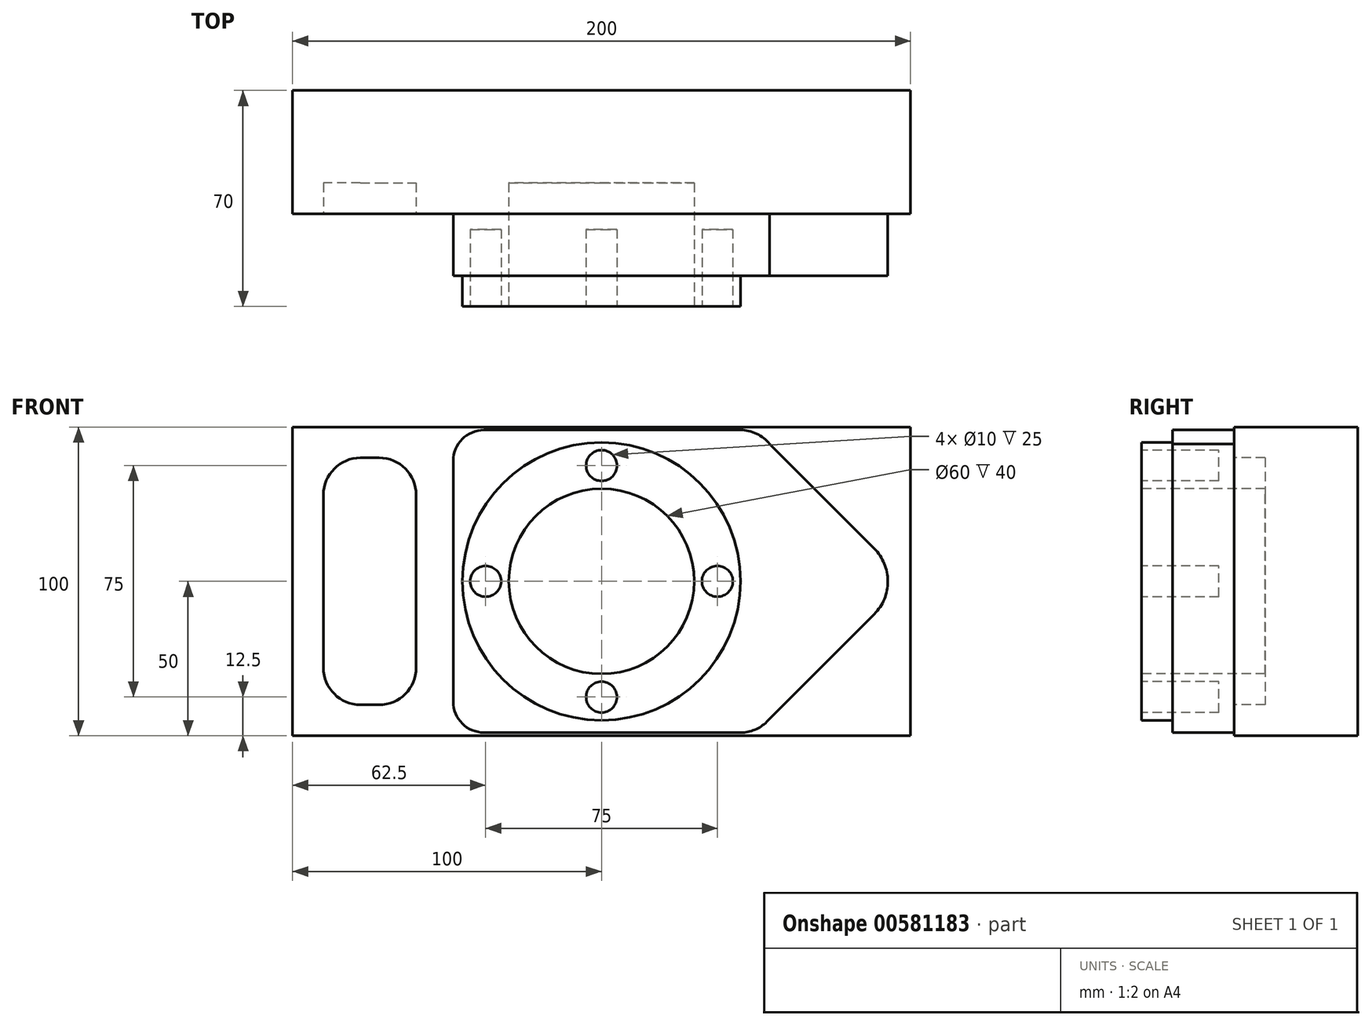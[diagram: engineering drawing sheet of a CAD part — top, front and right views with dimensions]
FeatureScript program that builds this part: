
annotation { "Feature Type Name" : "Feature", "Feature Type Description" : "" }
export const myFeature = defineFeature(function(context is Context, id is Id, definition is map)
    precondition{}
    {
        {
            var Q0;
            Q0=qCreatedBy(makeId("Front.planeOp"),FACE);
            var sketch = newSketch(context, id + "F0", { "sketchPlane" : qUnion([Q0])});
            skLineSegment(sketch, "E0.bottom", {"start": v(0, 0) * mm, "end": v(-200, 0) * mm});
            skLineSegment(sketch, "E0.top", {"start": v(0, 100) * mm, "end": v(-200, 100) * mm});
            skLineSegment(sketch, "E0.left", {"start": v(0, 0) * mm, "end": v(0, 100) * mm});
            skLineSegment(sketch, "E0.right", {"start": v(-200, 0) * mm, "end": v(-200, 100) * mm});
            skSolve(sketch);
        }
        {
            var Q0;
            Q0=makeQuery(id+"F0.imprint","IMPRINT",FACE,{"disambiguationData":[TD([[makeQuery(id+"F0.imprint","IMPRINT",EDGE,{"derivedFrom":sQuery(id+"F0.wireOp",EDGE,"E0.bottom")}),-1.0]])]});
            extrude(context, id + "F1", {"entities" : qUnion([Q0]), "depth" : 40 * mm, "offsetDistance" : 25 * mm});
        }
        {
            var Q0;
            Q0=makeQuery(id+"F1.opExtrude","CAP_FACE",FACE,{"disambiguationData":[OSD([sQuery(id+"F0.wireOp",EDGE,"E0.bottom"),sQuery(id+"F0.wireOp",EDGE,"E0.top"),sQuery(id+"F0.wireOp",EDGE,"E0.left"),sQuery(id+"F0.wireOp",EDGE,"E0.right")])],"isStart":false});
            var sketch = newSketch(context, id + "F2", { "sketchPlane" : qUnion([Q0])});
            skCircle(sketch, "E1", {"center": v(-100, 50) * mm, "radius": 30 * mm});
            skLineSegment(sketch, "E2.bottom", {"start": v(-178, 90) * mm, "end": v(-172, 90) * mm});
            skLineSegment(sketch, "E2.top", {"start": v(-178, 10) * mm, "end": v(-172, 10) * mm});
            skLineSegment(sketch, "E2.left", {"start": v(-190, 78) * mm, "end": v(-190, 22) * mm});
            skLineSegment(sketch, "E2.right", {"start": v(-160, 78) * mm, "end": v(-160, 22) * mm});
            skPoint(sketch, "E3.visualSharp", {"position": v(-190, 90) * mm});
            skArc(sketch, "E3.filletArc", {"start": v(-178, 90) * mm, "mid": v(-186.49, 86.49) * mm, "end": v(-190, 78) * mm});
            skPoint(sketch, "E4.visualSharp", {"position": v(-160, 90) * mm});
            skArc(sketch, "E4.filletArc", {"start": v(-160, 78) * mm, "mid": v(-163.51, 86.49) * mm, "end": v(-172, 90) * mm});
            skPoint(sketch, "E5.visualSharp", {"position": v(-190, 10) * mm});
            skArc(sketch, "E5.filletArc", {"start": v(-190, 22) * mm, "mid": v(-186.49, 13.51) * mm, "end": v(-178, 10) * mm});
            skPoint(sketch, "E6.visualSharp", {"position": v(-160, 10) * mm});
            skArc(sketch, "E6.filletArc", {"start": v(-172, 10) * mm, "mid": v(-163.51, 13.51) * mm, "end": v(-160, 22) * mm});
            skSolve(sketch);
        }
        {
            var Q0;
            Q0=makeQuery(id+"F2.imprint","IMPRINT",FACE,{"disambiguationData":[TD([[makeQuery(id+"F2.imprint","IMPRINT",EDGE,{"derivedFrom":sQuery(id+"F2.wireOp",EDGE,"E2.bottom")}),-1.0]])]});
            var Q1;
            Q1=makeQuery(id+"F2.imprint","IMPRINT",FACE,{"disambiguationData":[TD([[makeQuery(id+"F2.imprint","IMPRINT",EDGE,{"derivedFrom":sQuery(id+"F2.wireOp",EDGE,"E1")}),1.0]])]});
            extrude(context, id + "F3", {"entities" : qUnion([Q0, Q1]), "operationType" : NewBodyOperationType.REMOVE, "oppositeDirection" : true, "depth" : 10 * mm, "offsetDistance" : 25 * mm});
        }
        {
            var Q0;
            Q0=makeQuery(id+"F1.opExtrude","CAP_FACE",FACE,{"disambiguationData":[OSD([sQuery(id+"F0.wireOp",EDGE,"E0.bottom"),sQuery(id+"F0.wireOp",EDGE,"E0.top"),sQuery(id+"F0.wireOp",EDGE,"E0.left"),sQuery(id+"F0.wireOp",EDGE,"E0.right")])],"isStart":false});
            var sketch = newSketch(context, id + "F4", { "sketchPlane" : qUnion([Q0])});
            skLineSegment(sketch, "E7", {"start": v(-148, 89) * mm, "end": v(-148, 11) * mm});
            skLineSegment(sketch, "E8", {"start": v(-138, 99) * mm, "end": v(-54.98, 99) * mm});
            skLineSegment(sketch, "E9", {"start": v(-138, 1) * mm, "end": v(-54.98, 1) * mm});
            skArc(sketch, "E10", {"start": v(-138, 99) * mm, "mid": v(-145.07, 96.07) * mm, "end": v(-148, 89) * mm});
            skArc(sketch, "E11", {"start": v(-148, 11) * mm, "mid": v(-145.07, 3.93) * mm, "end": v(-138, 1) * mm});
            skLineSegment(sketch, "E12", {"start": v(-46.49, 4.52) * mm, "end": v(-11.7, 39.4) * mm});
            skArc(sketch, "E13", {"start": v(-45.6, 94.48) * mm, "mid": v(-49.78, 97.81) * mm, "end": v(-54.98, 99) * mm});
            skArc(sketch, "E14", {"start": v(-54.98, 1) * mm, "mid": v(-50.38, 1.92) * mm, "end": v(-46.49, 4.52) * mm});
            skArc(sketch, "E15", {"start": v(-11.7, 39.4) * mm, "mid": v(-7.32, 50) * mm, "end": v(-11.73, 60.6) * mm});
            skLineSegment(sketch, "E16", {"start": v(-45.6, 94.49) * mm, "end": v(-11.73, 60.6) * mm});
            skSolve(sketch);
        }
        {
            var Q0;
            Q0=makeQuery(id+"F4.imprint","IMPRINT",FACE,{"disambiguationData":[TD([[makeQuery(id+"F4.imprint","IMPRINT",EDGE,{"derivedFrom":sQuery(id+"F4.wireOp",EDGE,"E7")}),1.0]])]});
            extrude(context, id + "F5", {"entities" : qUnion([Q0]), "operationType" : NewBodyOperationType.ADD, "depth" : 20 * mm, "offsetDistance" : 25 * mm});
        }
        {
            var Q0;
            Q0=makeQuery(id+"F5.opExtrude","CAP_FACE",FACE,{"disambiguationData":[OSD([sQuery(id+"F2.wireOp",EDGE,"E1"),sQuery(id+"F4.wireOp",EDGE,"E7"),sQuery(id+"F4.wireOp",EDGE,"E8"),sQuery(id+"F4.wireOp",EDGE,"E9"),sQuery(id+"F4.wireOp",EDGE,"E10"),sQuery(id+"F4.wireOp",EDGE,"E11"),sQuery(id+"F4.wireOp",EDGE,"E12"),sQuery(id+"F4.wireOp",EDGE,"E13"),sQuery(id+"F4.wireOp",EDGE,"E14"),sQuery(id+"F4.wireOp",EDGE,"E15"),sQuery(id+"F4.wireOp",EDGE,"E16")])],"isStart":false});
            var sketch = newSketch(context, id + "F6", { "sketchPlane" : qUnion([Q0])});
            skCircle(sketch, "E17", {"center": v(-100, 50) * mm, "radius": 45 * mm});
            skCircle(sketch, "E18", {"center": v(-100, 50) * mm, "radius": 30 * mm});
            skSolve(sketch);
        }
        {
            var Q0;
            Q0=makeQuery(id+"F6.imprint","IMPRINT",FACE,{"disambiguationData":[TD([[makeQuery(id+"F6.imprint","IMPRINT",EDGE,{"derivedFrom":sQuery(id+"F6.wireOp",EDGE,"E17")}),1.0]])]});
            extrude(context, id + "F7", {"entities" : qUnion([Q0]), "operationType" : NewBodyOperationType.ADD, "depth" : 10 * mm, "offsetDistance" : 25 * mm});
        }
        {
            var Q0;
            Q0=makeQuery(id+"F7.opExtrude","CAP_FACE",FACE,{"disambiguationData":[OSD([sQuery(id+"F6.wireOp",EDGE,"E17"),sQuery(id+"F6.wireOp",EDGE,"E18")])],"isStart":false});
            var sketch = newSketch(context, id + "F8", { "sketchPlane" : qUnion([Q0])});
            skCircle(sketch, "E19", {"center": v(-100, 50) * mm, "radius": 37.5 * mm, "construction": true});
            skCircle(sketch, "E20", {"center": v(-100, 87.5) * mm, "radius": 5 * mm});
            skCircle(sketch, "E21", {"center": v(-137.5, 50) * mm, "radius": 5 * mm});
            skCircle(sketch, "E22", {"center": v(-62.5, 50) * mm, "radius": 5 * mm});
            skCircle(sketch, "E23", {"center": v(-100, 12.5) * mm, "radius": 5 * mm});
            skSolve(sketch);
        }
        {
            var Q0;
            Q0=makeQuery(id+"F8.imprint","IMPRINT",FACE,{"disambiguationData":[TD([[makeQuery(id+"F8.imprint","IMPRINT",EDGE,{"derivedFrom":sQuery(id+"F8.wireOp",EDGE,"E20")}),1.0]])]});
            var Q1;
            Q1=makeQuery(id+"F8.imprint","IMPRINT",FACE,{"disambiguationData":[TD([[makeQuery(id+"F8.imprint","IMPRINT",EDGE,{"derivedFrom":sQuery(id+"F8.wireOp",EDGE,"E21")}),1.0]])]});
            var Q2;
            Q2=makeQuery(id+"F8.imprint","IMPRINT",FACE,{"disambiguationData":[TD([[makeQuery(id+"F8.imprint","IMPRINT",EDGE,{"derivedFrom":sQuery(id+"F8.wireOp",EDGE,"E23")}),1.0]])]});
            var Q3;
            Q3=makeQuery(id+"F8.imprint","IMPRINT",FACE,{"disambiguationData":[TD([[makeQuery(id+"F8.imprint","IMPRINT",EDGE,{"derivedFrom":sQuery(id+"F8.wireOp",EDGE,"E22")}),1.0]])]});
            extrude(context, id + "F9", {"entities" : qUnion([Q0, Q1, Q2, Q3]), "operationType" : NewBodyOperationType.REMOVE, "oppositeDirection" : true, "depth" : 25 * mm, "offsetDistance" : 25 * mm});
        }
    });
